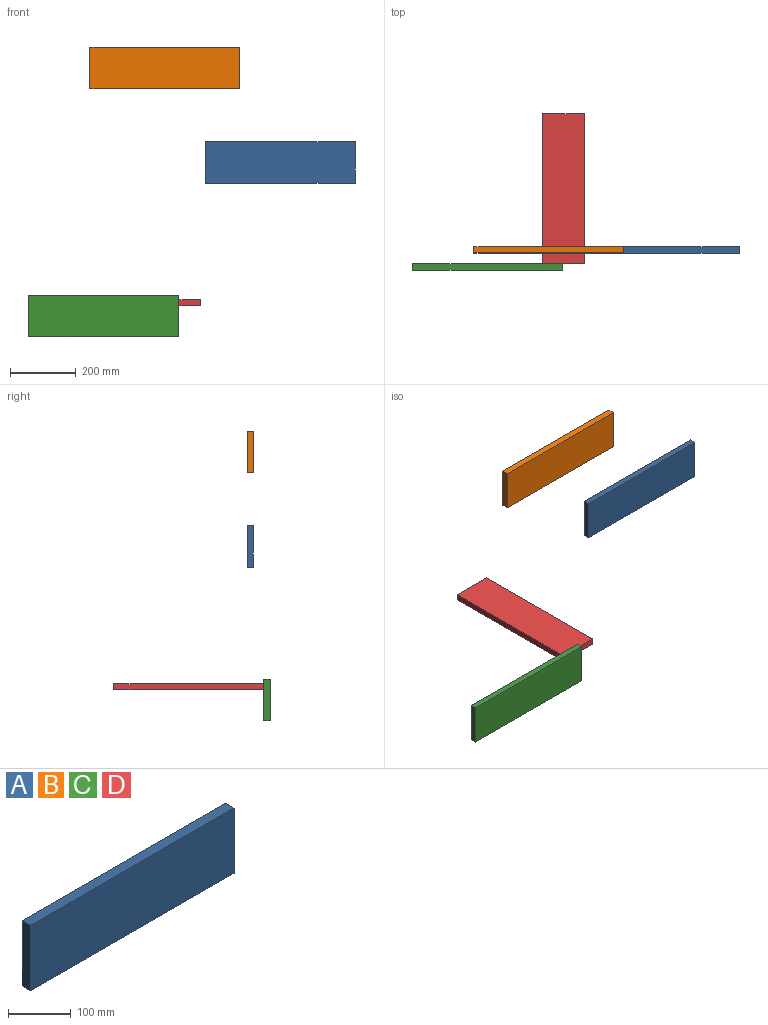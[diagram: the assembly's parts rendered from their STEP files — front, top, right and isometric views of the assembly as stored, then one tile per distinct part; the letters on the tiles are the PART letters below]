
ASSEMBLY  parts=4 mates=1
PART A: 6 faces, bbox 457.2x19.1x127 mm
  f0: plane 457.2x19.05mm, normal (0,0,1), area 8709.7mm2, adj f1,f3,f4,f5
  f1: plane 127x19.05mm, normal (-1,0,0), area 2419.3mm2, adj f0,f2,f4,f5
  f2: plane 457.2x19.05mm, normal (0,0,-1), area 8709.7mm2, adj f1,f3,f4,f5
  f3: plane 127x19.05mm, normal (1,0,0), area 2419.3mm2, adj f0,f2,f4,f5
  f4: plane 457.2x127mm, normal (0,-1,0), area 58064.4mm2, adj f0,f1,f2,f3
  f5: plane 457.2x127mm, normal (0,1,0), area 58064.4mm2, adj f0,f1,f2,f3
PART B: same geometry as A
PART C: same geometry as A
PART D: same geometry as A
PLACE A t=(351.6,0,713.87)mm
PLACE B t=(0,0,1001.55)mm
PLACE C t=(-186.66,-50.73,245.58)mm fixed
PLACE D rot(axis=(0.58,0.58,0.58),120deg) t=(-25.89,157.86,385.89)mm
MATE planar D.f1 <-> C.f5  axis (0,-1,0) through (64.26,-50.73,366.84)mm
